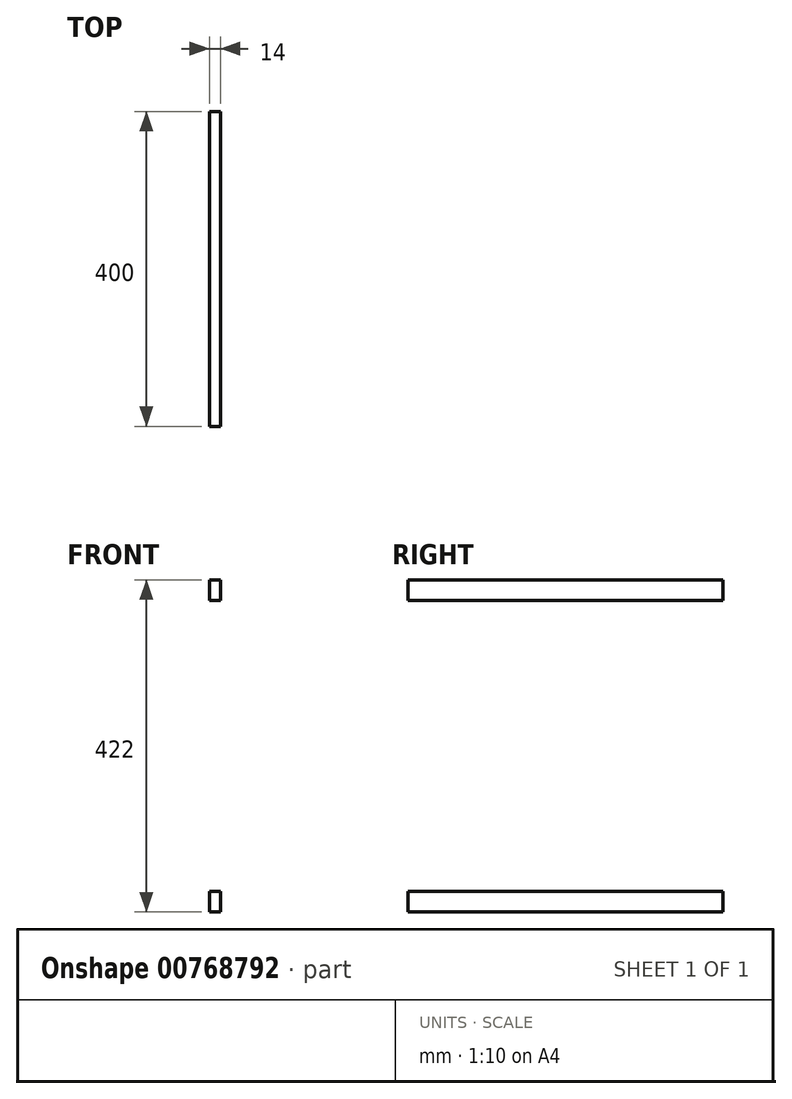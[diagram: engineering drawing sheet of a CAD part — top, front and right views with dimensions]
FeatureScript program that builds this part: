
annotation { "Feature Type Name" : "Feature", "Feature Type Description" : "" }
export const myFeature = defineFeature(function(context is Context, id is Id, definition is map)
    precondition{}
    {
        {
            var Q0;
            Q0=qCreatedBy(makeId("Front.planeOp"),FACE);
            var sketch = newSketch(context, id + "F0", { "sketchPlane" : qUnion([Q0])});
            skLineSegment(sketch, "E0.bottom", {"start": v(-17.06, 281.02) * mm, "end": v(-3.06, 281.02) * mm});
            skLineSegment(sketch, "E0.top", {"start": v(-17.06, 255.02) * mm, "end": v(-3.06, 255.02) * mm});
            skLineSegment(sketch, "E0.left", {"start": v(-17.06, 281.02) * mm, "end": v(-17.06, 255.02) * mm});
            skLineSegment(sketch, "E0.right", {"start": v(-3.06, 281.02) * mm, "end": v(-3.06, 255.02) * mm});
            skLineSegment(sketch, "E1.bottom", {"start": v(-17.06, -114.98) * mm, "end": v(-3.06, -114.98) * mm});
            skLineSegment(sketch, "E1.top", {"start": v(-17.06, -140.98) * mm, "end": v(-3.06, -140.98) * mm});
            skLineSegment(sketch, "E1.left", {"start": v(-17.06, -114.98) * mm, "end": v(-17.06, -140.98) * mm});
            skLineSegment(sketch, "E1.right", {"start": v(-3.06, -114.98) * mm, "end": v(-3.06, -140.98) * mm});
            skLineSegment(sketch, "E2", {"start": v(-37.06, 981.02) * mm, "end": v(8.12, 981.02) * mm});
            skLineSegment(sketch, "E3", {"start": v(8.12, 981.02) * mm, "end": v(34, -120.98) * mm});
            skLineSegment(sketch, "E4", {"start": v(-37.06, 981.02) * mm, "end": v(-37.06, 255.02) * mm});
            skLineSegment(sketch, "E5", {"start": v(-3.06, -200.98) * mm, "end": v(76.94, -200.98) * mm});
            skLineSegment(sketch, "E6", {"start": v(76.94, -200.98) * mm, "end": v(74.68, -105.02) * mm});
            skLineSegment(sketch, "E7", {"start": v(74.68, -105.02) * mm, "end": v(51.64, -105.56) * mm});
            skLineSegment(sketch, "E8", {"start": v(51.64, -105.56) * mm, "end": v(51.99, -120.56) * mm});
            skLineSegment(sketch, "E9", {"start": v(51.99, -120.56) * mm, "end": v(34, -120.98) * mm});
            skLineSegment(sketch, "E10", {"start": v(-3.06, 255.02) * mm, "end": v(-3.06, 229.02) * mm});
            skLineSegment(sketch, "E11", {"start": v(-3.06, 229.02) * mm, "end": v(-37.06, 229.02) * mm});
            skLineSegment(sketch, "E12", {"start": v(-17.06, 255.02) * mm, "end": v(-37.06, 255.02) * mm});
            skLineSegment(sketch, "E13.trimOffspring", {"start": v(-37.06, 229.02) * mm, "end": v(-37.06, -140.98) * mm});
            skLineSegment(sketch, "E14", {"start": v(-17.06, -140.98) * mm, "end": v(-37.06, -140.98) * mm});
            skLineSegment(sketch, "E15", {"start": v(-3.06, -140.98) * mm, "end": v(-3.06, -166.98) * mm});
            skLineSegment(sketch, "E16", {"start": v(-3.06, -166.98) * mm, "end": v(-37.06, -166.98) * mm});
            skLineSegment(sketch, "E17", {"start": v(-37.06, -166.98) * mm, "end": v(-37.06, -200.98) * mm});
            skLineSegment(sketch, "E18", {"start": v(-37.06, -200.98) * mm, "end": v(-3.06, -200.98) * mm});
            skSolve(sketch);
        }
        {
            var Q0;
            Q0=makeQuery(id+"F0.imprint","IMPRINT",FACE,{"disambiguationData":[TD([[makeQuery(id+"F0.imprint","IMPRINT",EDGE,{"derivedFrom":sQuery(id+"F0.wireOp",EDGE,"E1.bottom")}),-1.0]])]});
            var Q1;
            Q1=makeQuery(id+"F0.imprint","IMPRINT",FACE,{"disambiguationData":[TD([[makeQuery(id+"F0.imprint","IMPRINT",EDGE,{"derivedFrom":sQuery(id+"F0.wireOp",EDGE,"E0.bottom")}),-1.0]])]});
            extrude(context, id + "F1", {"entities" : qUnion([Q0, Q1]), "endBound" : BoundingType.SYMMETRIC, "depth" : 400 * mm, "offsetDistance" : 25 * mm});
        }
    });
